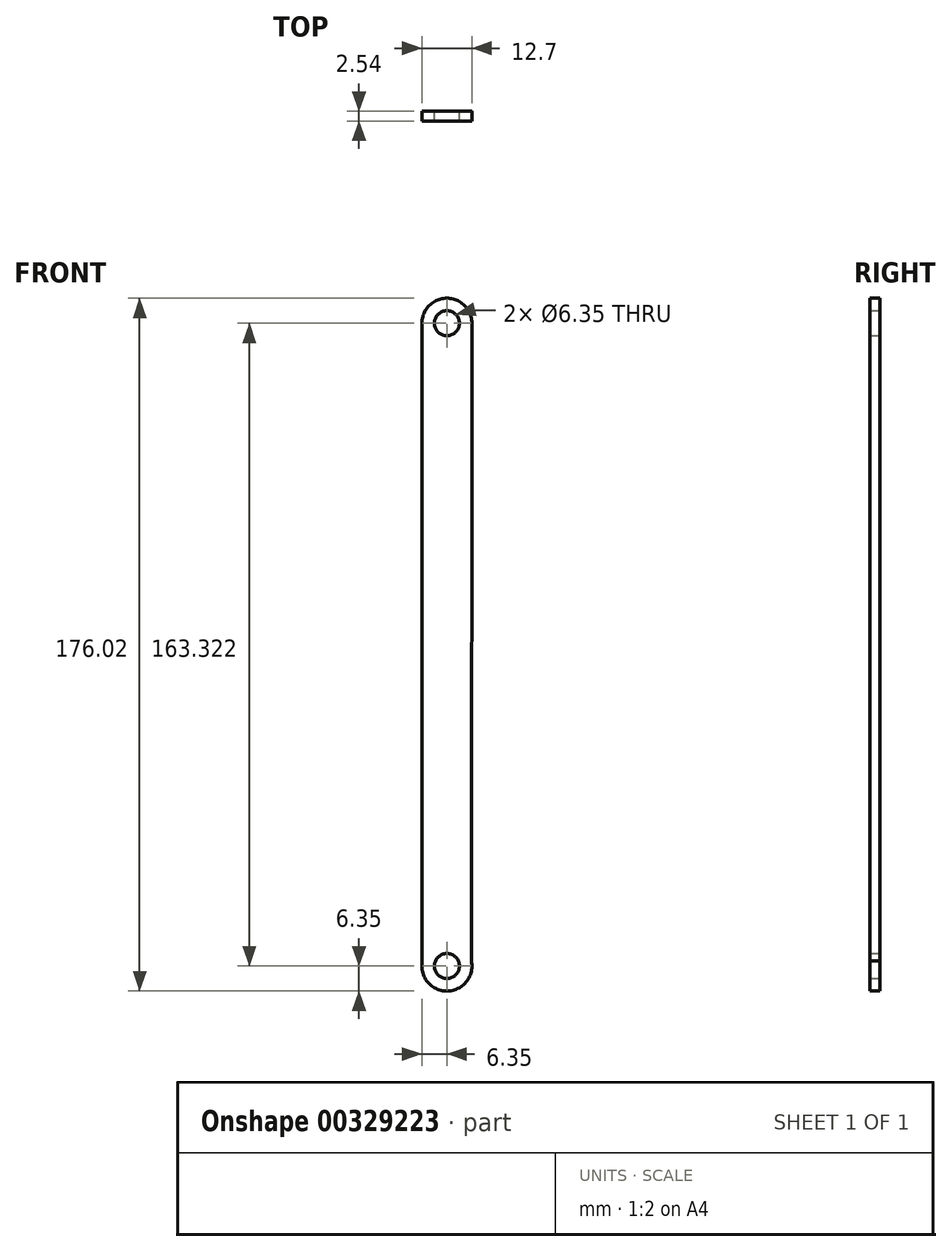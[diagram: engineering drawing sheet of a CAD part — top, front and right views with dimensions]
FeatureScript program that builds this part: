
annotation { "Feature Type Name" : "Feature", "Feature Type Description" : "" }
export const myFeature = defineFeature(function(context is Context, id is Id, definition is map)
    precondition{}
    {
        {
            var Q0;
            Q0=qCreatedBy(makeId("Front.planeOp"),FACE);
            var sketch = newSketch(context, id + "F0", { "sketchPlane" : qUnion([Q0])});
            skCircle(sketch, "E0", {"center": v(0, 0) * mm, "radius": 3.18 * mm});
            skCircle(sketch, "E1", {"center": v(0, 163.32) * mm, "radius": 6.35 * mm});
            skCircle(sketch, "E2", {"center": v(0, 163.32) * mm, "radius": 3.18 * mm});
            skCircle(sketch, "E3", {"center": v(0, 0) * mm, "radius": 6.35 * mm});
            skLineSegment(sketch, "E4", {"start": v(-6.35, 163.32) * mm, "end": v(-6.35, 0) * mm});
            skLineSegment(sketch, "E5", {"start": v(6.35, 163.32) * mm, "end": v(6.22, 1.3) * mm});
            skSolve(sketch);
        }
        {
            var Q0;
            Q0=makeQuery(id+"F0.imprint","IMPRINT",FACE,{"disambiguationData":[TD([[makeQuery(id+"F0.imprint","IMPRINT",EDGE,{"derivedFrom":sQuery(id+"F0.wireOp",EDGE,"E0")}),-1.0]])]});
            var Q1;
            {var subQ0=sQuery(id+"F0.wireOp",EDGE,"E4");Q1=makeQuery(id+"F0.imprint","IMPRINT",FACE,{"disambiguationData":[TD([[makeQuery(id+"F0.imprint","IMPRINT",EDGE,{"derivedFrom":subQ0}),1.0]])]});}
            var Q2;
            Q2=makeQuery(id+"F0.imprint","IMPRINT",FACE,{"disambiguationData":[TD([[makeQuery(id+"F0.imprint","IMPRINT",EDGE,{"derivedFrom":sQuery(id+"F0.wireOp",EDGE,"E2")}),-1.0]])]});
            extrude(context, id + "F1", {"entities" : qUnion([Q0, Q1, Q2]), "depth" : 2.54 * mm});
        }
    });
